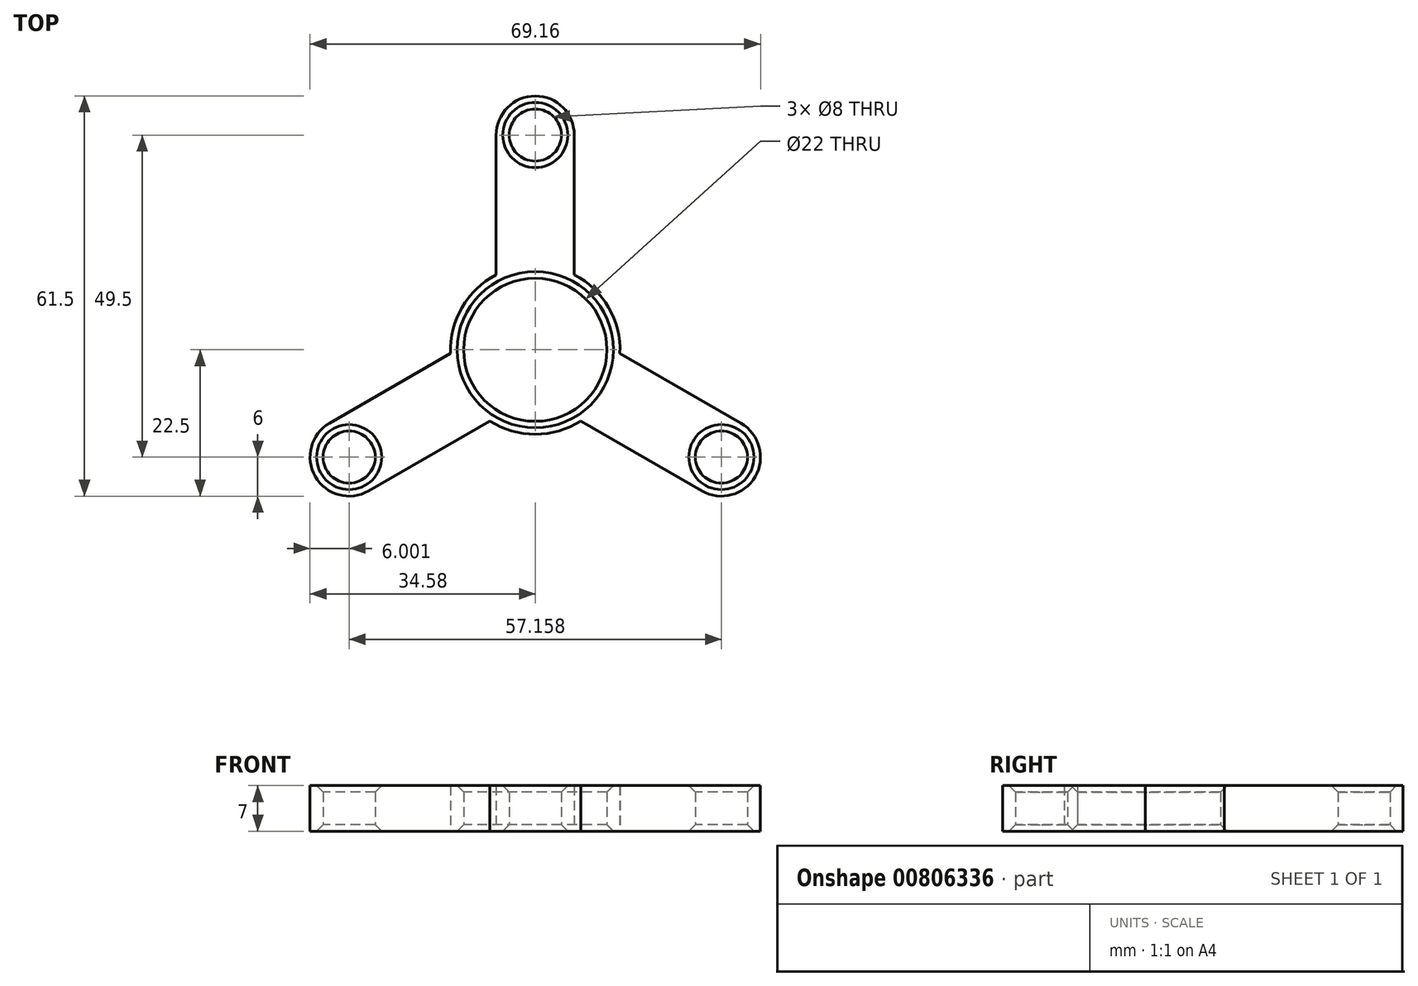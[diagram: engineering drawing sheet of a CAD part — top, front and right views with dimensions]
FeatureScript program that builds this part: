
annotation { "Feature Type Name" : "Feature", "Feature Type Description" : "" }
export const myFeature = defineFeature(function(context is Context, id is Id, definition is map)
    precondition{}
    {
        {
            var Q0;
            Q0=qCreatedBy(makeId("Top.planeOp"),FACE);
            var sketch = newSketch(context, id + "F0", { "sketchPlane" : qUnion([Q0])});
            skCircle(sketch, "E0", {"center": v(0, 0) * mm, "radius": 11 * mm});
            skCircle(sketch, "E1", {"center": v(0, 0) * mm, "radius": 13 * mm});
            skCircle(sketch, "E2", {"center": v(0, 33) * mm, "radius": 4 * mm});
            skCircle(sketch, "E3", {"center": v(0, 33) * mm, "radius": 6 * mm});
            skPoint(sketch, "E4.center", {"position": v(0, 0.5) * mm});
            skCircle(sketch, "E5.1.0", {"center": v(-28.58, -16.5) * mm, "radius": 6 * mm});
            skCircle(sketch, "E5.1.1", {"center": v(-28.58, -16.5) * mm, "radius": 4 * mm});
            skCircle(sketch, "E5.2.0", {"center": v(28.58, -16.5) * mm, "radius": 6 * mm});
            skCircle(sketch, "E5.2.1", {"center": v(28.58, -16.5) * mm, "radius": 4 * mm});
            skLineSegment(sketch, "E6", {"start": v(-6, 33) * mm, "end": v(-6, 11.53) * mm});
            skLineSegment(sketch, "E7", {"start": v(6, 33) * mm, "end": v(6, 11.53) * mm});
            skLineSegment(sketch, "E8.1.0", {"start": v(-25.58, -21.7) * mm, "end": v(-6.99, -10.96) * mm});
            skLineSegment(sketch, "E8.1.1", {"start": v(-31.58, -11.3) * mm, "end": v(-12.99, -0.57) * mm});
            skLineSegment(sketch, "E8.2.0", {"start": v(31.58, -11.3) * mm, "end": v(12.99, -0.57) * mm});
            skLineSegment(sketch, "E8.2.1", {"start": v(25.58, -21.7) * mm, "end": v(6.99, -10.96) * mm});
            skSolve(sketch);
        }
        {
            var Q0;
            Q0=makeQuery(id+"F0.imprint","IMPRINT",FACE,{"disambiguationData":[TD([[makeQuery(id+"F0.imprint","IMPRINT",EDGE,{"derivedFrom":sQuery(id+"F0.wireOp",EDGE,"E1")}),-1.0]])]});
            var Q1;
            Q1=makeQuery(id+"F0.imprint","IMPRINT",FACE,{"disambiguationData":[TD([[makeQuery(id+"F0.imprint","IMPRINT",EDGE,{"derivedFrom":sQuery(id+"F0.wireOp",EDGE,"c202e4ac-ae93-4b29-baa2-4fd0cf997ff0.1.0")}),-1.0]])]});
            var Q2;
            Q2=makeQuery(id+"F0.imprint","IMPRINT",FACE,{"disambiguationData":[TD([[makeQuery(id+"F0.imprint","IMPRINT",EDGE,{"derivedFrom":sQuery(id+"F0.wireOp",EDGE,"E0")}),-1.0]])]});
            var Q3;
            Q3=makeQuery(id+"F0.imprint","IMPRINT",FACE,{"disambiguationData":[TD([[makeQuery(id+"F0.imprint","IMPRINT",EDGE,{"derivedFrom":sQuery(id+"F0.wireOp",EDGE,"E2")}),-1.0]])]});
            var Q4;
            Q4=makeQuery(id+"F0.imprint","IMPRINT",FACE,{"disambiguationData":[TD([[makeQuery(id+"F0.imprint","IMPRINT",EDGE,{"derivedFrom":sQuery(id+"F0.wireOp",EDGE,"c202e4ac-ae93-4b29-baa2-4fd0cf997ff0.2.0")}),-1.0]])]});
            var Q5;
            Q5=makeQuery(id+"F0.imprint","IMPRINT",FACE,{"disambiguationData":[TD([[makeQuery(id+"F0.imprint","IMPRINT",EDGE,{"derivedFrom":sQuery(id+"F0.wireOp",EDGE,"0e0c9052-6751-44d5-bc73-aae295e7aca2.2.0")}),-1.0]])]});
            var Q6;
            Q6=makeQuery(id+"F0.imprint","IMPRINT",FACE,{"disambiguationData":[TD([[makeQuery(id+"F0.imprint","IMPRINT",EDGE,{"derivedFrom":sQuery(id+"F0.wireOp",EDGE,"0e0c9052-6751-44d5-bc73-aae295e7aca2.4.0")}),-1.0]])]});
            var Q7;
            Q7=makeQuery(id+"F0.imprint","IMPRINT",FACE,{"disambiguationData":[TD([[makeQuery(id+"F0.imprint","IMPRINT",EDGE,{"derivedFrom":sQuery(id+"F0.wireOp",EDGE,"6d77e2d1-ec52-477d-ae8a-bde1fbb15b47.4.1")}),-1.0]])]});
            var Q8;
            Q8=makeQuery(id+"F0.imprint","IMPRINT",FACE,{"disambiguationData":[TD([[makeQuery(id+"F0.imprint","IMPRINT",EDGE,{"derivedFrom":sQuery(id+"F0.wireOp",EDGE,"6d77e2d1-ec52-477d-ae8a-bde1fbb15b47.2.1")}),-1.0]])]});
            var Q9;
            Q9=makeQuery(id+"F0.imprint","IMPRINT",FACE,{"disambiguationData":[TD([[makeQuery(id+"F0.imprint","IMPRINT",EDGE,{"derivedFrom":sQuery(id+"F0.wireOp",EDGE,"3cc0715d-66bc-4789-9b96-2980e166defb.4.1")}),-1.0]])]});
            var Q10;
            Q10=makeQuery(id+"F0.imprint","IMPRINT",FACE,{"disambiguationData":[TD([[makeQuery(id+"F0.imprint","IMPRINT",EDGE,{"derivedFrom":sQuery(id+"F0.wireOp",EDGE,"3cc0715d-66bc-4789-9b96-2980e166defb.2.1")}),-1.0]])]});
            var Q11;
            Q11=makeQuery(id+"F0.imprint","IMPRINT",FACE,{"disambiguationData":[TD([[makeQuery(id+"F0.imprint","IMPRINT",EDGE,{"derivedFrom":sQuery(id+"F0.wireOp",EDGE,"E5.1.1")}),-1.0]])]});
            var Q12;
            Q12=makeQuery(id+"F0.imprint","IMPRINT",FACE,{"disambiguationData":[TD([[makeQuery(id+"F0.imprint","IMPRINT",EDGE,{"derivedFrom":sQuery(id+"F0.wireOp",EDGE,"E5.2.1")}),-1.0]])]});
            extrude(context, id + "F1", {"entities" : qUnion([Q0, Q1, Q2, Q3, Q4, Q5, Q6, Q7, Q8, Q9, Q10, Q11, Q12]), "endBound" : BoundingType.SYMMETRIC, "depth" : 7 * mm, "offsetDistance" : 25.4 * mm});
        }
        {
            var Q0;
            Q0=makeQuery(id+"F1.opExtrude","CAP_EDGE",EDGE,{"disambiguationData":[OSD([sQuery(id+"F0.wireOp",EDGE,"E2")])],"isStart":false});
            var Q1;
            Q1=makeQuery(id+"F1.opExtrude","CAP_EDGE",EDGE,{"disambiguationData":[OSD([sQuery(id+"F0.wireOp",EDGE,"E0")])],"isStart":false});
            var Q2;
            Q2=makeQuery(id+"F1.opExtrude","CAP_EDGE",EDGE,{"disambiguationData":[OSD([sQuery(id+"F0.wireOp",EDGE,"E5.1.1")])],"isStart":false});
            var Q3;
            Q3=makeQuery(id+"F1.opExtrude","CAP_EDGE",EDGE,{"disambiguationData":[OSD([sQuery(id+"F0.wireOp",EDGE,"E5.2.1")])],"isStart":false});
            var Q4;
            Q4=makeQuery(id+"F1.opExtrude","CAP_EDGE",EDGE,{"disambiguationData":[OSD([sQuery(id+"F0.wireOp",EDGE,"E5.1.1")])],"isStart":true});
            var Q5;
            Q5=makeQuery(id+"F1.opExtrude","CAP_EDGE",EDGE,{"disambiguationData":[OSD([sQuery(id+"F0.wireOp",EDGE,"E0")])],"isStart":true});
            var Q6;
            Q6=makeQuery(id+"F1.opExtrude","CAP_EDGE",EDGE,{"disambiguationData":[OSD([sQuery(id+"F0.wireOp",EDGE,"E5.2.1")])],"isStart":true});
            var Q7;
            Q7=makeQuery(id+"F1.opExtrude","CAP_EDGE",EDGE,{"disambiguationData":[OSD([sQuery(id+"F0.wireOp",EDGE,"E2")])],"isStart":true});
            chamfer(context, id + "F2", {"entities" : qUnion([Q0, Q1, Q2, Q3, Q4, Q5, Q6, Q7]), "width" : 1 * mm, "tangentPropagation" : true});
        }
    });
